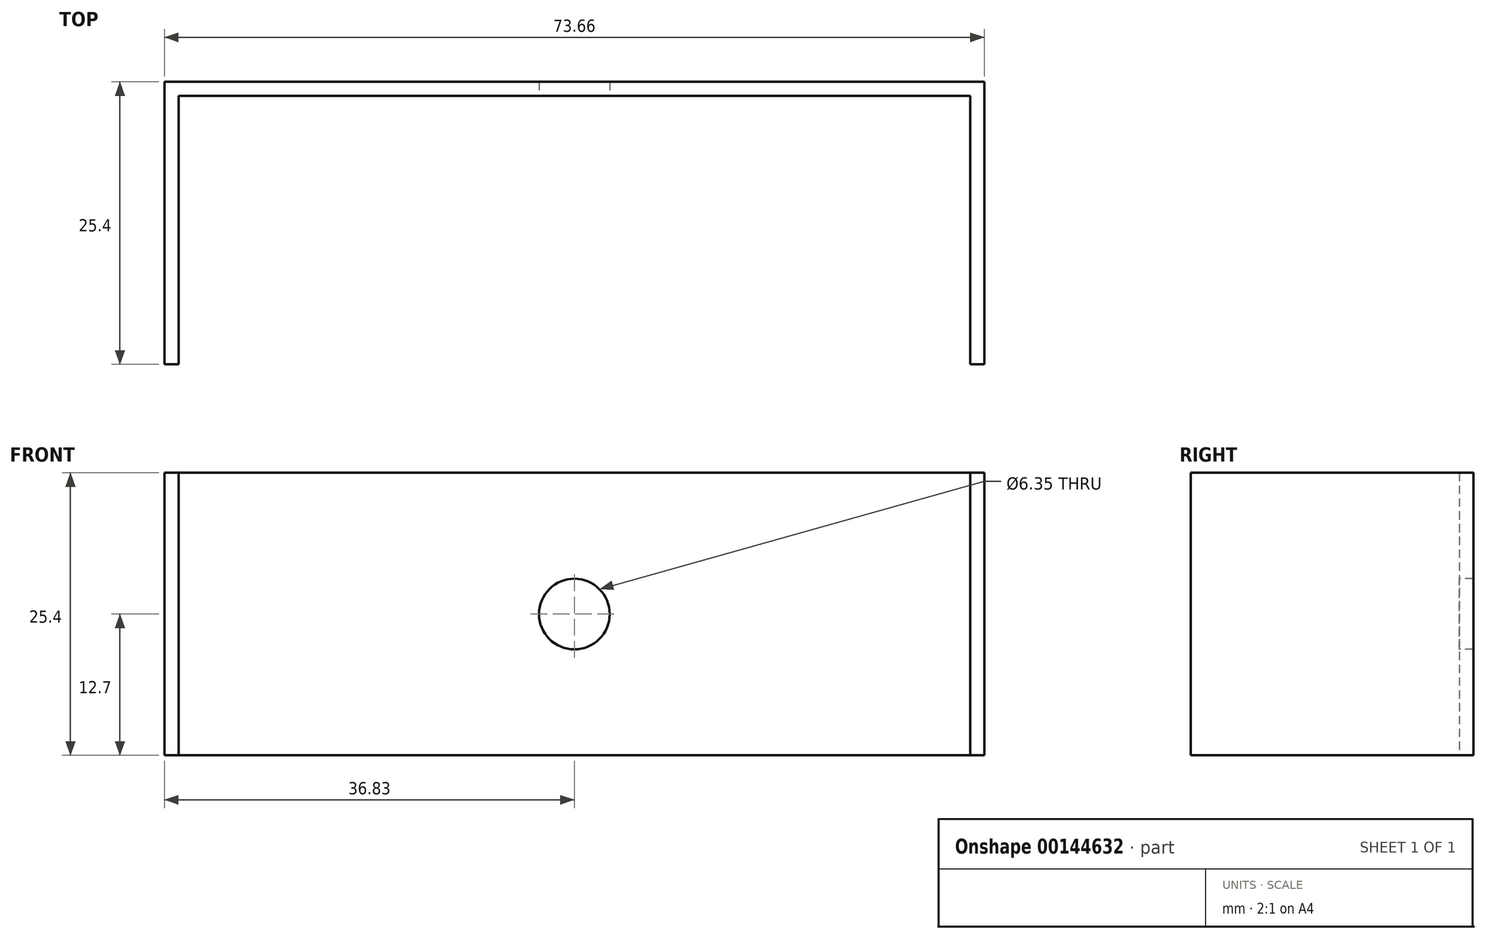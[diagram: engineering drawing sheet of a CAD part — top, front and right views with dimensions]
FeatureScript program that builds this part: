
annotation { "Feature Type Name" : "Feature", "Feature Type Description" : "" }
export const myFeature = defineFeature(function(context is Context, id is Id, definition is map)
    precondition{}
    {
        {
            var Q0;
            Q0=qCreatedBy(makeId("Top.planeOp"),FACE);
            var sketch = newSketch(context, id + "F0", { "sketchPlane" : qUnion([Q0])});
            skLineSegment(sketch, "E0.top", {"start": v(36.83, 12.7) * mm, "end": v(-36.83, 12.7) * mm});
            skLineSegment(sketch, "E0.left", {"start": v(36.83, -12.7) * mm, "end": v(36.83, 12.7) * mm});
            skLineSegment(sketch, "E0.right", {"start": v(-36.83, -12.7) * mm, "end": v(-36.83, 12.7) * mm});
            skPoint(sketch, "E0.middle", {"position": v(0, 0) * mm});
            skLineSegment(sketch, "E1.0", {"start": v(35.56, -12.7) * mm, "end": v(35.56, 11.43) * mm});
            skLineSegment(sketch, "E1.1", {"start": v(35.56, 11.43) * mm, "end": v(-35.56, 11.43) * mm});
            skLineSegment(sketch, "E1.2", {"start": v(-35.56, -12.7) * mm, "end": v(-35.56, 11.43) * mm});
            skLineSegment(sketch, "E2", {"start": v(-36.83, -12.7) * mm, "end": v(-35.56, -12.7) * mm});
            skLineSegment(sketch, "E3", {"start": v(35.56, -12.7) * mm, "end": v(36.83, -12.7) * mm});
            skSolve(sketch);
        }
        {
            var Q0;
            Q0=makeQuery(id+"F0.imprint","IMPRINT",FACE,{"disambiguationData":[TD([[makeQuery(id+"F0.imprint","IMPRINT",EDGE,{"derivedFrom":sQuery(id+"F0.wireOp",EDGE,"E0.top")}),1.0]])]});
            var Q1;
            Q1 = qSketchRegion(id + "F2", true);
            extrude(context, id + "F1", {"entities" : qUnion([Q0, Q1]), "endBound" : BoundingType.SYMMETRIC, "depth" : 25.4 * mm});
        }
        {
            var Q0;
            Q0=makeQuery(id+"F1.opExtrude","SWEPT_FACE",FACE,{"disambiguationData":[OSD([sQuery(id+"F0.wireOp",EDGE,"E1.1")])]});
            var sketch = newSketch(context, id + "F2", { "sketchPlane" : qUnion([Q0])});
            skCircle(sketch, "E4", {"center": v(0, 0) * mm, "radius": 3.3 * mm});
            skSolve(sketch);
        }
        {
            var Q0;
            Q0=sQuery(id+"F2.wireOp",VERTEX,"E4.center");
            var Q1;
            Q1=makeQuery(id+"F1.opExtrude","SWEPT_BODY",BODY,{"disambiguationData":[OSD([sQuery(id+"F0.wireOp",EDGE,"E0.top"),sQuery(id+"F0.wireOp",EDGE,"E0.left"),sQuery(id+"F0.wireOp",EDGE,"E0.right"),sQuery(id+"F0.wireOp",EDGE,"E1.0"),sQuery(id+"F0.wireOp",EDGE,"E1.1"),sQuery(id+"F0.wireOp",EDGE,"E1.2"),sQuery(id+"F0.wireOp",EDGE,"E2"),sQuery(id+"F0.wireOp",EDGE,"E3")])]});
            hole(context, id + "F3", {"style" : HoleStyle.SIMPLE, "endStyle" : HoleEndStyle.BLIND, "holeDiameter" : 6.35 * mm, "holeDepth" : 12.7 * mm, "startFromSketch" : true, "locations" : qUnion([Q0]), "scope" : qUnion([Q1])});
        }
    });
